# Revit family: Faucet-Deck_Mount-Bath-KOHLER-FINIAL-K-8673X
name_source: partatom
category: Plumbing Fixtures
revit_build: Autodesk Revit 2017 (Build: 20160225_1515(x64)
units: mm (PartAtom-declared; Revit-internal decimal feet)

## family parameters
Cut with Voids When Loaded = No
Host = Face
OmniClass Number = 23.31.11.00
OmniClass Title = Faucets
Part Type = Normal
Room Calculation Point = No
Round Connector Dimension = Use Diameter
Shared = No

## types (2) — shared parameters
ADA Compliant = No
Assembly Code = D2010
CW Connection = Yes
Cold Water Inlet = Cold Water Inlet
Date Modified = 09/28/2020
Default Elevation = 36"
Drain Included = No
Finish = Kohler-Metal-CP-Polished_Chrome
Flow Rate = 0 GPM
HW Connection = Yes
Handle Clearance = 3 13/16"
Height = 9 13/16"
Hot Water Inlet = Hot Water Inlet
Length = 7 1/2"
Manufacturer = KOHLER Co.
Master Format 2014 = 22 41 39
Master Format 2014 Name = Residential Faucets, Supplies, and Trim
Material = Brass construction
Pressure = 0.00 psi
Product Documentation Link = http://resources.kohler.com
Product Name = FINIAL
Product Page URL = https://www.kohler.co.th
Spout Reach = 7 1/2"
URL = https://www.kohler.co.th
Vent Connection = No
Waste Connection = No
Waste Water Outlet = Waste Water Outlet
WaterSense Certified = No

## per-type parameters (varying)
| type | Description | Handle finish | Model | Type |
| Lever handle,CP- Polished chrome | Bath And Deck-Mount Faucet, Traditional Lever Handles | Kohler-Metal-CP-Polished_Chrome | K-8673X-4M-CP | 1 |
| Lever Handles With White Accents, CP- Polished chrome | Bath And Deck-Mount Faucet, Lever Handles With White Accents | Kohler-Plastic-0-White | K-8673X-4P-CP | 2 |

## geometry (parser evidence)
native form markers: Sweep x6
no freeform markers — native parametric forms only
